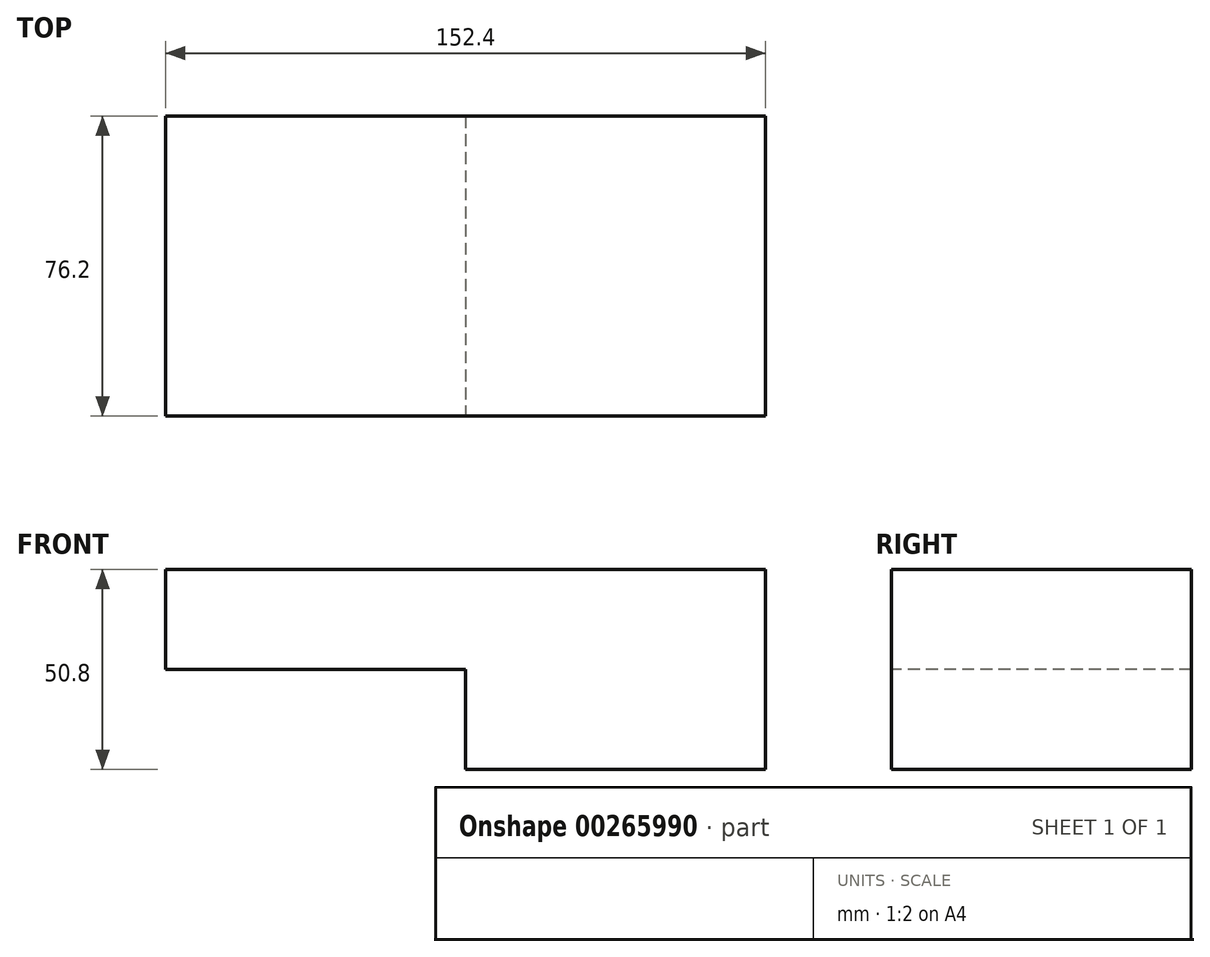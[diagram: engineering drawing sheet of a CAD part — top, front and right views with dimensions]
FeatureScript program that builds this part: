
annotation { "Feature Type Name" : "Feature", "Feature Type Description" : "" }
export const myFeature = defineFeature(function(context is Context, id is Id, definition is map)
    precondition{}
    {
        {
            var Q0;
            Q0=qCreatedBy(makeId("Front.planeOp"),FACE);
            var sketch = newSketch(context, id + "F0", { "sketchPlane" : qUnion([Q0])});
            skLineSegment(sketch, "E0.bottom", {"start": v(-76.23, 1.04) * mm, "end": v(76.17, 1.04) * mm});
            skLineSegment(sketch, "E0.top", {"start": v(-76.23, -49.76) * mm, "end": v(76.17, -49.76) * mm});
            skLineSegment(sketch, "E0.left", {"start": v(-76.23, 1.04) * mm, "end": v(-76.23, -49.76) * mm});
            skLineSegment(sketch, "E0.right", {"start": v(76.17, 1.04) * mm, "end": v(76.17, -49.76) * mm});
            skSolve(sketch);
        }
        {
            var Q0;
            Q0 = qSketchRegion(id + "F0", true);
            extrude(context, id + "F1", {"entities" : qUnion([Q0]), "depth" : 76.2 * mm});
        }
        {
            var Q0;
            Q0=makeQuery(id+"F1.opExtrude","CAP_FACE",FACE,{"disambiguationData":[OSD([sQuery(id+"F0.wireOp",EDGE,"E0.bottom"),sQuery(id+"F0.wireOp",EDGE,"E0.top"),sQuery(id+"F0.wireOp",EDGE,"E0.left"),sQuery(id+"F0.wireOp",EDGE,"E0.right")])],"isStart":false});
            var sketch = newSketch(context, id + "F2", { "sketchPlane" : qUnion([Q0])});
            skLineSegment(sketch, "E1.bottom", {"start": v(-76.23, -49.76) * mm, "end": v(-0.03, -49.76) * mm});
            skLineSegment(sketch, "E1.top", {"start": v(-76.23, -24.36) * mm, "end": v(-0.03, -24.36) * mm});
            skLineSegment(sketch, "E1.left", {"start": v(-76.23, -49.76) * mm, "end": v(-76.23, -24.36) * mm});
            skLineSegment(sketch, "E1.right", {"start": v(-0.03, -49.76) * mm, "end": v(-0.03, -24.36) * mm});
            skSolve(sketch);
        }
        {
            var Q0;
            Q0=makeQuery(id+"F2.imprint","IMPRINT",FACE,{"disambiguationData":[TD([[makeQuery(id+"F2.imprint","IMPRINT",EDGE,{"derivedFrom":sQuery(id+"F2.wireOp",EDGE,"E1.bottom")}),1.0]])]});
            extrude(context, id + "F3", {"entities" : qUnion([Q0]), "operationType" : NewBodyOperationType.REMOVE, "endBound" : BoundingType.UP_TO_NEXT, "oppositeDirection" : true, "depth" : 25.4 * mm});
        }
    });
